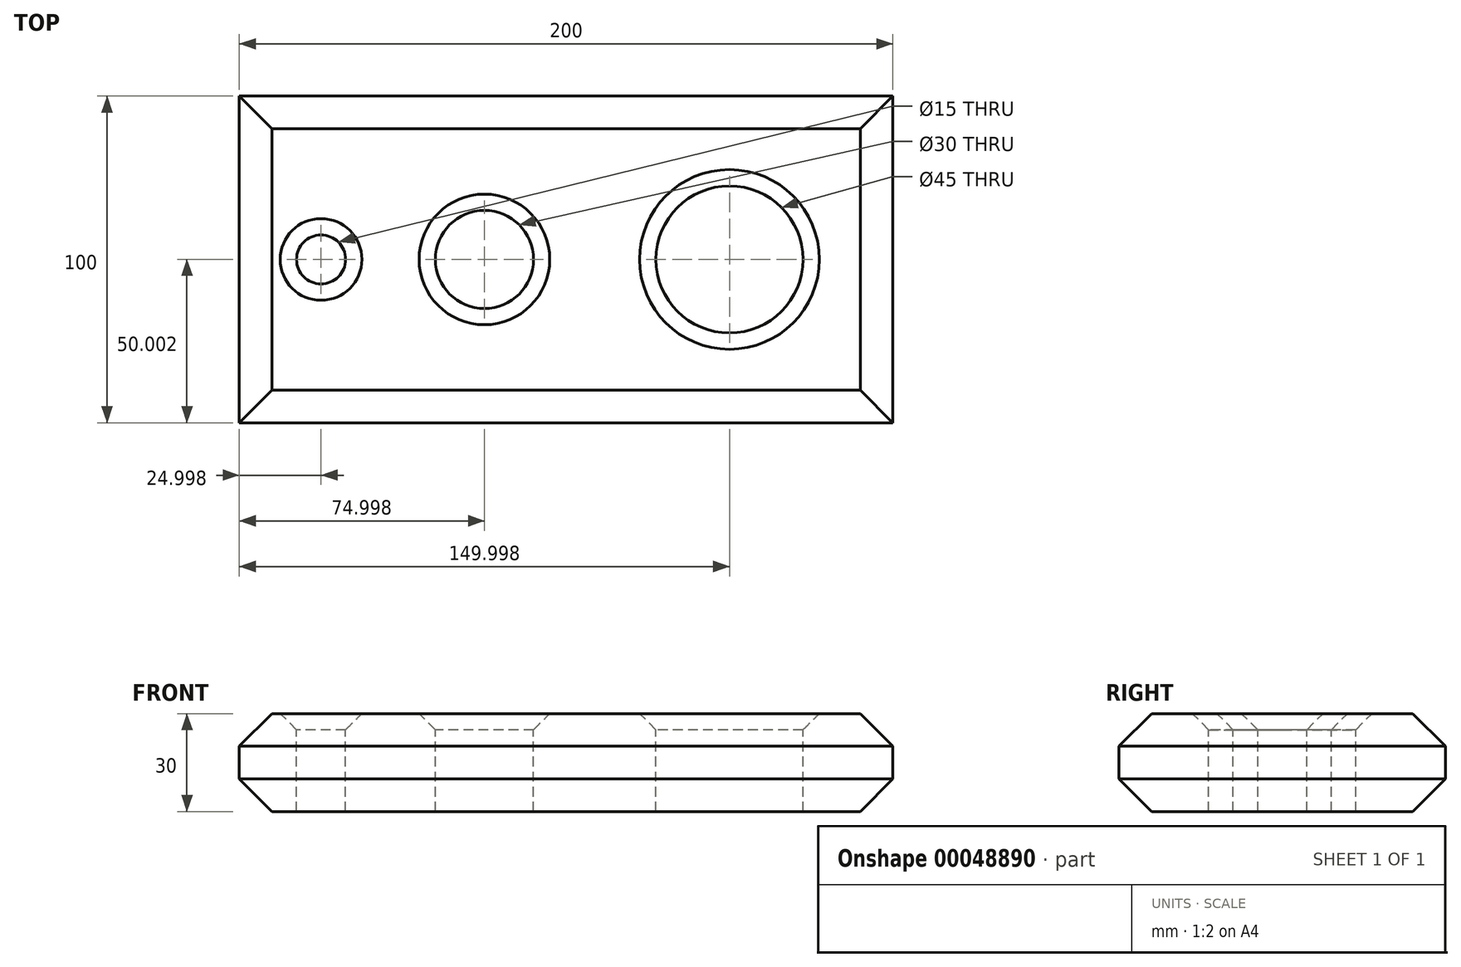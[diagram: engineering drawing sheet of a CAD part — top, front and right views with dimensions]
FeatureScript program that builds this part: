
annotation { "Feature Type Name" : "Feature", "Feature Type Description" : "" }
export const myFeature = defineFeature(function(context is Context, id is Id, definition is map)
    precondition{}
    {
        {
            var Q0;
            Q0=qCreatedBy(makeId("Top.planeOp"),FACE);
            var sketch = newSketch(context, id + "F0", { "sketchPlane" : qUnion([Q0])});
            skLineSegment(sketch, "E0.bottom", {"start": v(-129.42, 59.46) * mm, "end": v(70.58, 59.46) * mm});
            skLineSegment(sketch, "E0.top", {"start": v(-129.42, -40.54) * mm, "end": v(70.58, -40.54) * mm});
            skLineSegment(sketch, "E0.left", {"start": v(-129.42, 59.46) * mm, "end": v(-129.42, -40.54) * mm});
            skLineSegment(sketch, "E0.right", {"start": v(70.58, 59.46) * mm, "end": v(70.58, -40.54) * mm});
            skLineSegment(sketch, "E1", {"start": v(-129.42, -40.54) * mm, "end": v(-129.42, 9.46) * mm, "construction": true});
            skCircle(sketch, "E2", {"center": v(-104.42, 9.46) * mm, "radius": 7.5 * mm});
            skCircle(sketch, "E3", {"center": v(-54.42, 9.46) * mm, "radius": 15 * mm});
            skCircle(sketch, "E4", {"center": v(20.58, 9.46) * mm, "radius": 22.5 * mm});
            skSolve(sketch);
        }
        {
            var Q0;
            Q0=makeQuery(id+"F0.imprint","IMPRINT",FACE,{"disambiguationData":[TD([[makeQuery(id+"F0.imprint","IMPRINT",EDGE,{"derivedFrom":sQuery(id+"F0.wireOp",EDGE,"E0.bottom")}),-1.0]])]});
            extrude(context, id + "F1", {"entities" : qUnion([Q0]), "oppositeDirection" : true, "depth" : 30 * mm});
        }
        {
            var Q0;
            Q0=makeQuery(id+"F1.opExtrude","CAP_EDGE",EDGE,{"disambiguationData":[OSD([sQuery(id+"F0.wireOp",EDGE,"E2")])],"isStart":true});
            chamfer(context, id + "F2", {"entities" : qUnion([Q0]), "chamferType" : ChamferType.OFFSET_ANGLE, "width" : 5 * mm, "oppositeDirection" : false, "angle" : 45 * degree, "tangentPropagation" : true});
        }
        {
            var Q0;
            Q0=makeQuery(id+"F1.opExtrude","CAP_EDGE",EDGE,{"disambiguationData":[OSD([sQuery(id+"F0.wireOp",EDGE,"E3")])],"isStart":true});
            chamfer(context, id + "F3", {"entities" : qUnion([Q0]), "chamferType" : ChamferType.OFFSET_ANGLE, "width" : 5 * mm, "oppositeDirection" : false, "angle" : 45 * degree, "tangentPropagation" : true});
        }
        {
            var Q0;
            Q0=makeQuery(id+"F1.opExtrude","CAP_EDGE",EDGE,{"disambiguationData":[OSD([sQuery(id+"F0.wireOp",EDGE,"E4")])],"isStart":true});
            chamfer(context, id + "F4", {"entities" : qUnion([Q0]), "chamferType" : ChamferType.OFFSET_ANGLE, "width" : 5 * mm, "oppositeDirection" : false, "angle" : 45 * degree, "tangentPropagation" : true});
        }
        {
            var Q0;
            Q0=makeQuery(id+"F1.opExtrude","CAP_EDGE",EDGE,{"disambiguationData":[OSD([sQuery(id+"F0.wireOp",EDGE,"E0.right")])],"isStart":true});
            chamfer(context, id + "F5", {"entities" : qUnion([Q0]), "chamferType" : ChamferType.OFFSET_ANGLE, "width" : 10 * mm, "oppositeDirection" : false, "angle" : 45 * degree, "tangentPropagation" : true});
        }
        {
            var Q0;
            Q0=makeQuery(id+"F1.opExtrude","CAP_EDGE",EDGE,{"disambiguationData":[OSD([sQuery(id+"F0.wireOp",EDGE,"E0.right")])],"isStart":false});
            chamfer(context, id + "F6", {"entities" : qUnion([Q0]), "chamferType" : ChamferType.OFFSET_ANGLE, "width" : 10 * mm, "oppositeDirection" : false, "angle" : 45 * degree, "tangentPropagation" : true});
        }
        {
            var Q0;
            Q0=makeQuery(id+"F1.opExtrude","CAP_EDGE",EDGE,{"disambiguationData":[OSD([sQuery(id+"F0.wireOp",EDGE,"E0.left")])],"isStart":true});
            chamfer(context, id + "F7", {"entities" : qUnion([Q0]), "chamferType" : ChamferType.OFFSET_ANGLE, "width" : 10 * mm, "oppositeDirection" : false, "angle" : 45 * degree, "tangentPropagation" : true});
        }
        {
            var Q0;
            Q0=makeQuery(id+"F1.opExtrude","CAP_EDGE",EDGE,{"disambiguationData":[OSD([sQuery(id+"F0.wireOp",EDGE,"E0.left")])],"isStart":false});
            chamfer(context, id + "F8", {"entities" : qUnion([Q0]), "chamferType" : ChamferType.OFFSET_ANGLE, "width" : 10 * mm, "oppositeDirection" : false, "angle" : 45 * degree, "tangentPropagation" : true});
        }
        {
            var Q0;
            Q0=makeQuery(id+"F1.opExtrude","CAP_EDGE",EDGE,{"disambiguationData":[OSD([sQuery(id+"F0.wireOp",EDGE,"E0.top")])],"isStart":true});
            chamfer(context, id + "F9", {"entities" : qUnion([Q0]), "chamferType" : ChamferType.OFFSET_ANGLE, "width" : 10 * mm, "oppositeDirection" : false, "angle" : 45 * degree, "tangentPropagation" : true});
        }
        {
            var Q0;
            Q0=makeQuery(id+"F1.opExtrude","CAP_EDGE",EDGE,{"disambiguationData":[OSD([sQuery(id+"F0.wireOp",EDGE,"E0.bottom")])],"isStart":false});
            chamfer(context, id + "F10", {"entities" : qUnion([Q0]), "chamferType" : ChamferType.OFFSET_ANGLE, "width" : 10 * mm, "oppositeDirection" : false, "angle" : 45 * degree, "tangentPropagation" : true});
        }
        {
            var Q0;
            Q0=makeQuery(id+"F1.opExtrude","CAP_EDGE",EDGE,{"disambiguationData":[OSD([sQuery(id+"F0.wireOp",EDGE,"E0.top")])],"isStart":false});
            chamfer(context, id + "F11", {"entities" : qUnion([Q0]), "chamferType" : ChamferType.OFFSET_ANGLE, "width" : 10 * mm, "oppositeDirection" : false, "angle" : 45 * degree, "tangentPropagation" : true});
        }
        {
            var Q0;
            Q0=makeQuery(id+"F1.opExtrude","CAP_EDGE",EDGE,{"disambiguationData":[OSD([sQuery(id+"F0.wireOp",EDGE,"E0.bottom")])],"isStart":true});
            chamfer(context, id + "F12", {"entities" : qUnion([Q0]), "chamferType" : ChamferType.OFFSET_ANGLE, "width" : 10 * mm, "oppositeDirection" : false, "angle" : 45 * degree, "tangentPropagation" : true});
        }
    });
